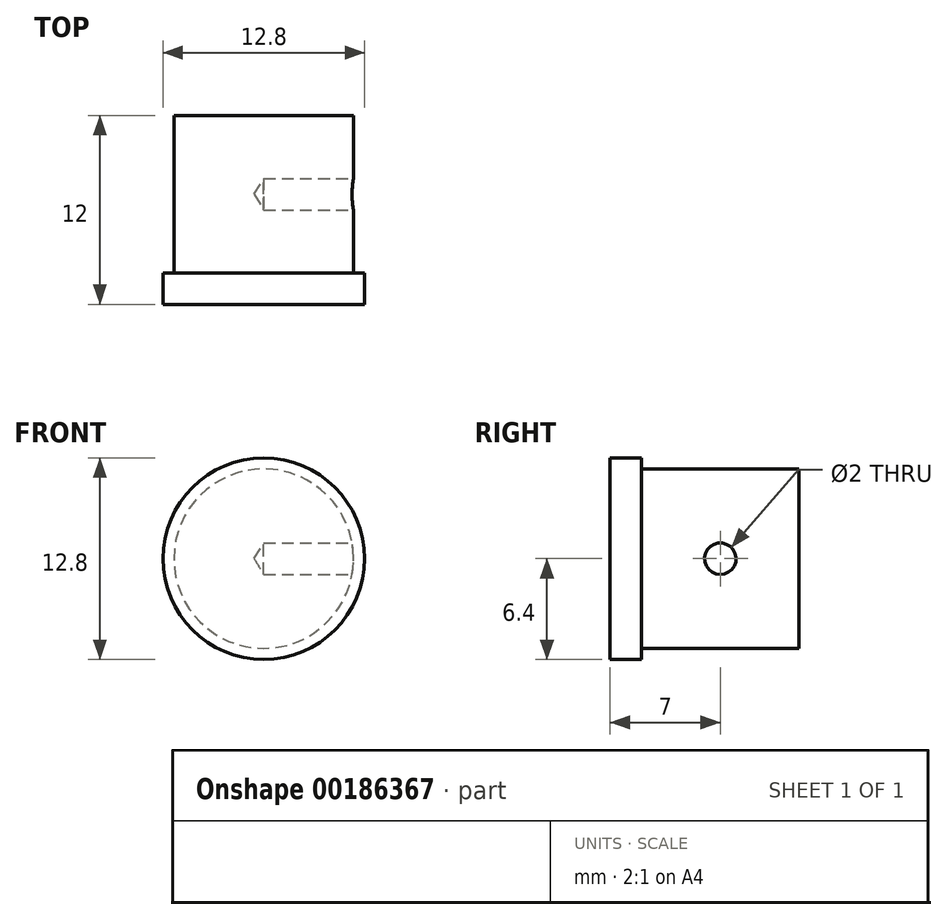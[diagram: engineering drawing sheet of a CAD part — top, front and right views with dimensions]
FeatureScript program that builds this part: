
annotation { "Feature Type Name" : "Feature", "Feature Type Description" : "" }
export const myFeature = defineFeature(function(context is Context, id is Id, definition is map)
    precondition{}
    {
        {
            assignVariable(context, id + "F0", {"name" : "OutDiam_Relief", "anyValue" : 11.4});
        }
        {
            assignVariable(context, id + "F1", {"name" : "InDiam_Hole", "anyValue" : 2});
        }
        {
            var Q0;
            Q0=qCreatedBy(makeId("Right.planeOp"),FACE);
            var sketch = newSketch(context, id + "F2", { "sketchPlane" : qUnion([Q0])});
            skLineSegment(sketch, "E0", {"start": v(11.47, 0) * mm, "end": v(0, 0) * mm, "construction": true});
            skLineSegment(sketch, "E1", {"start": v(12, 0) * mm, "end": v(12, 5.7) * mm});
            skLineSegment(sketch, "E2", {"start": v(2, 5.7) * mm, "end": v(12, 5.7) * mm});
            skLineSegment(sketch, "E3", {"start": v(2, 5.7) * mm, "end": v(2, 6.4) * mm});
            skLineSegment(sketch, "E4", {"start": v(0, 6.4) * mm, "end": v(2, 6.4) * mm});
            skLineSegment(sketch, "E5", {"start": v(0, 6.4) * mm, "end": v(0, 0) * mm});
            skLineSegment(sketch, "E6", {"start": v(0, 0) * mm, "end": v(12, 0) * mm});
            skSolve(sketch);
        }
        {
            var Q0;
            Q0=makeQuery(id+"F2.imprint","IMPRINT",FACE,{"disambiguationData":[TD([[makeQuery(id+"F2.imprint","IMPRINT",EDGE,{"derivedFrom":sQuery(id+"F2.wireOp",EDGE,"2muTHvRN-vOkX-I7TS-8VXv-9Uo2a6T2kHqg")}),-1.0]])]});
            var Q1;
            {var subQ4=sQuery(id+"F2.wireOp",EDGE,"vq0Eh5Rx-hKab-PJC6-916k-xS9uGsZsjFJb");Q1=makeQuery(id+"F2.imprint","IMPRINT",FACE,{"disambiguationData":[TD([[makeQuery(id+"F2.imprint","IMPRINT",EDGE,{"derivedFrom":subQ4}),1.0]])]});}
            var Q2;
            {var subQ2=sQuery(id+"F2.wireOp",EDGE,"E1");Q2=makeQuery(id+"F2.imprint","IMPRINT",FACE,{"disambiguationData":[TD([[makeQuery(id+"F2.imprint","IMPRINT",EDGE,{"derivedFrom":subQ2}),1.0]])]});}
            var Q3;
            Q3=sQuery(id+"F2.wireOp",EDGE,"E0");
            revolve(context, id + "F3", {"entities" : qUnion([Q0, Q1, Q2]), "axis" : qUnion([Q3]), "revolveType" : RevolveType.FULL});
        }
        {
            var Q0;
            Q0=qCreatedBy(makeId("Right.planeOp"),FACE);
            cPlane(context, id + "F4", {"entities" : qUnion([Q0]), "cplaneType" : CPlaneType.OFFSET, "offset" : (getVariable(context, 'OutDiam_Relief') / 2) * mm, "width" : 150 * mm, "height" : 150 * mm});
        }
        {
            var Q0;
            Q0=qCreatedBy(id+"F4.planeOp",FACE);
            var sketch = newSketch(context, id + "F5", { "sketchPlane" : qUnion([Q0])});
            skCircle(sketch, "E7", {"center": v(7, 0) * mm, "radius": 1 * mm});
            skLineSegment(sketch, "E8.0", {"start": v(2, 6.4) * mm, "end": v(2, -6.4) * mm});
            skPoint(sketch, "E9", {"position": v(2, 0) * mm});
            skSolve(sketch);
        }
        {
            var Q0;
            Q0=sQuery(id+"F5.wireOp",VERTEX,"E7.center");
            var Q1;
            Q1=makeQuery(id+"F3.opRevolve","SWEPT_BODY",BODY,{"disambiguationData":[OSD([sQuery(id+"F2.wireOp",EDGE,"E1"),sQuery(id+"F2.wireOp",EDGE,"E2"),sQuery(id+"F2.wireOp",EDGE,"E3"),sQuery(id+"F2.wireOp",EDGE,"E4"),sQuery(id+"F2.wireOp",EDGE,"E5"),sQuery(id+"F2.wireOp",EDGE,"vq0Eh5Rx-hKab-PJC6-916k-xS9uGsZsjFJb"),sQuery(id+"F2.wireOp",EDGE,"E6"),sQuery(id+"F2.wireOp",EDGE,"gCmW6R0u-Tpxj-T6pB-nSIk-QuKkspoCePad")])]});
            hole(context, id + "F6", {"style" : HoleStyle.SIMPLE, "endStyle" : HoleEndStyle.BLIND, "holeDiameter" : (getVariable(context, 'InDiam_Hole')) * mm, "holeDepth" : 5.7 * mm, "startFromSketch" : true, "locations" : qUnion([Q0]), "scope" : qUnion([Q1])});
        }
    });
